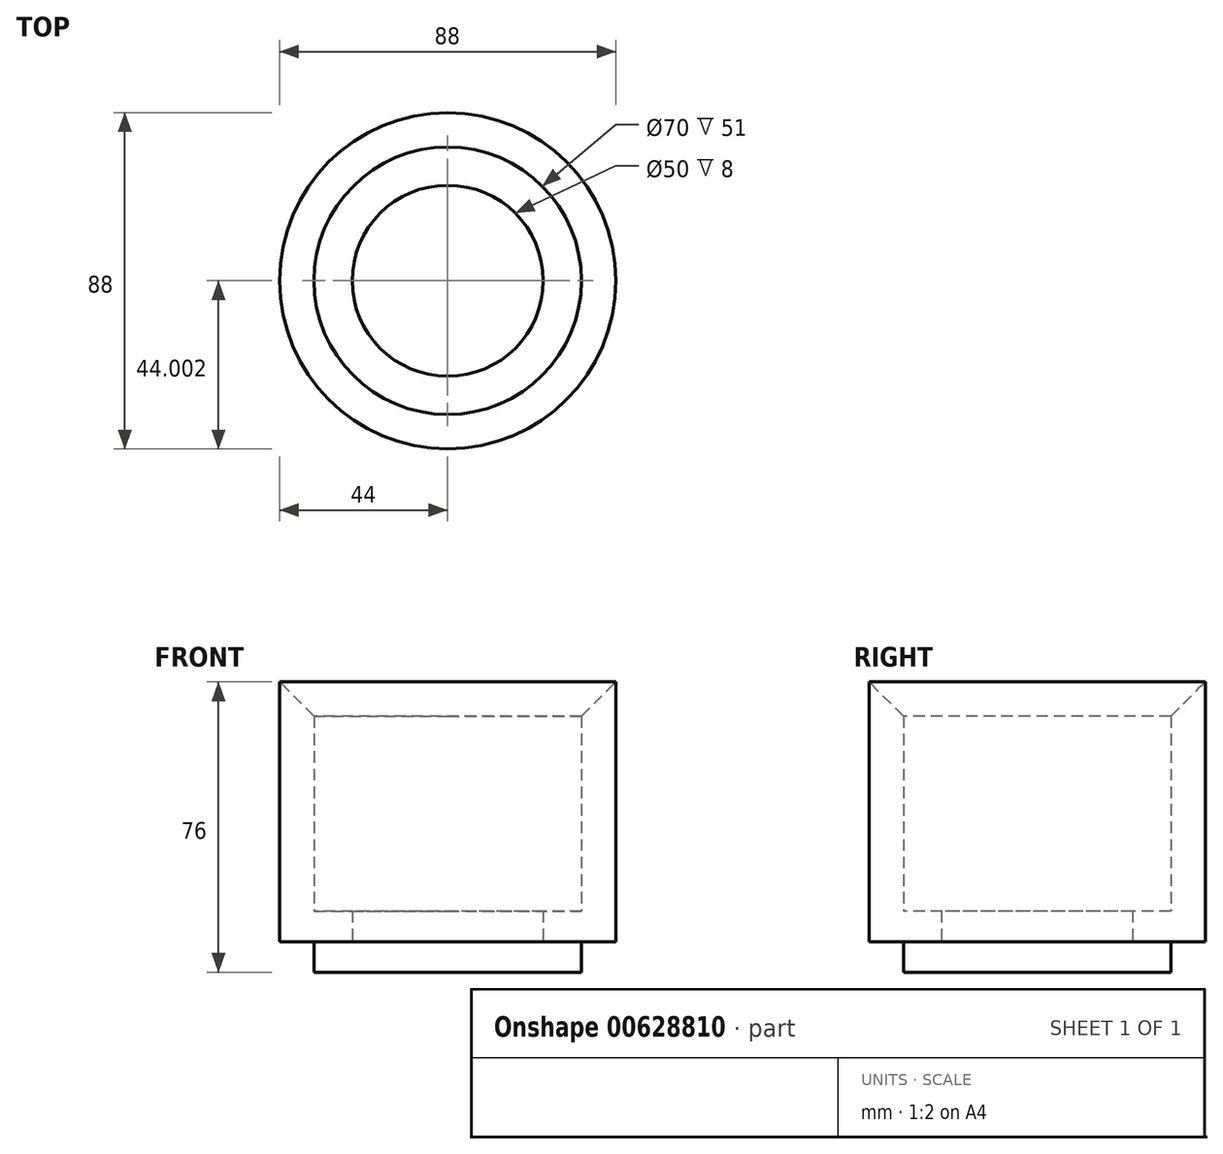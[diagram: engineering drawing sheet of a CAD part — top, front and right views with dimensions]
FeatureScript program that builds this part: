
annotation { "Feature Type Name" : "Feature", "Feature Type Description" : "" }
export const myFeature = defineFeature(function(context is Context, id is Id, definition is map)
    precondition{}
    {
        {
            var Q0;
            Q0=qCreatedBy(makeId("Right.planeOp"),FACE);
            var sketch = newSketch(context, id + "F0", { "sketchPlane" : qUnion([Q0])});
            skLineSegment(sketch, "E0", {"start": v(-37.85, 76.6) * mm, "end": v(-37.85, 16.6) * mm});
            skLineSegment(sketch, "E1", {"start": v(-37.85, 16.6) * mm, "end": v(-27.85, 16.6) * mm});
            skLineSegment(sketch, "E2", {"start": v(-27.85, 8.6) * mm, "end": v(-2.85, 8.6) * mm});
            skLineSegment(sketch, "E3", {"start": v(-37.85, 76.6) * mm, "end": v(-46.85, 76.6) * mm});
            skLineSegment(sketch, "E4", {"start": v(-46.85, 76.6) * mm, "end": v(-46.85, 8.6) * mm});
            skLineSegment(sketch, "E5", {"start": v(-46.85, 8.6) * mm, "end": v(-37.85, 8.6) * mm});
            skLineSegment(sketch, "E6", {"start": v(-37.85, 8.6) * mm, "end": v(-37.85, 0.6) * mm});
            skLineSegment(sketch, "E7", {"start": v(-37.85, 0.6) * mm, "end": v(-2.85, 0.6) * mm});
            skLineSegment(sketch, "E8", {"start": v(-2.85, 0.6) * mm, "end": v(-2.85, 8.6) * mm});
            skLineSegment(sketch, "E9", {"start": v(-27.85, 8.6) * mm, "end": v(-27.85, 16.6) * mm});
            skSolve(sketch);
        }
        {
            var Q0;
            Q0 = qSketchRegion(id + "F0", true);
            var Q1;
            Q1=sQuery(id+"F0.wireOp",EDGE,"E4");
            var Q2;
            Q2=sQuery(id+"F0.wireOp",EDGE,"E0");
            var Q3;
            Q3=sQuery(id+"F0.wireOp",EDGE,"E8");
            var Q4;
            Q4=sQuery(id+"F0.wireOp",EDGE,"E5");
            var Q5;
            Q5=sQuery(id+"F0.wireOp",EDGE,"E3");
            var Q6;
            Q6=sQuery(id+"F0.wireOp",EDGE,"E2");
            var Q7;
            Q7=sQuery(id+"F0.wireOp",EDGE,"E6");
            var Q8;
            Q8=sQuery(id+"F0.wireOp",EDGE,"E7");
            var Q9;
            Q9=sQuery(id+"F0.wireOp",EDGE,"E1");
            var Q10;
            Q10=sQuery(id+"F0.wireOp",EDGE,"E9");
            var Q11;
            Q11=sQuery(id+"F0.wireOp",EDGE,"E8");
            revolve(context, id + "F1", {"entities" : qUnion([Q0]), "surfaceEntities" : qUnion([Q1, Q2, Q3, Q4, Q5, Q6, Q7, Q8, Q9, Q10]), "axis" : qUnion([Q11]), "revolveType" : RevolveType.FULL});
        }
        {
            var Q0;
            Q0=makeQuery(id+"F1.opRevolve","SWEPT_EDGE",EDGE,{"disambiguationData":[OSD([sQuery(id+"F0.wireOp",EDGE,"E0"),sQuery(id+"F0.wireOp",EDGE,"E3")])]});
            chamfer(context, id + "F2", {"entities" : qUnion([Q0]), "width" : 9 * mm, "tangentPropagation" : true});
        }
    });
